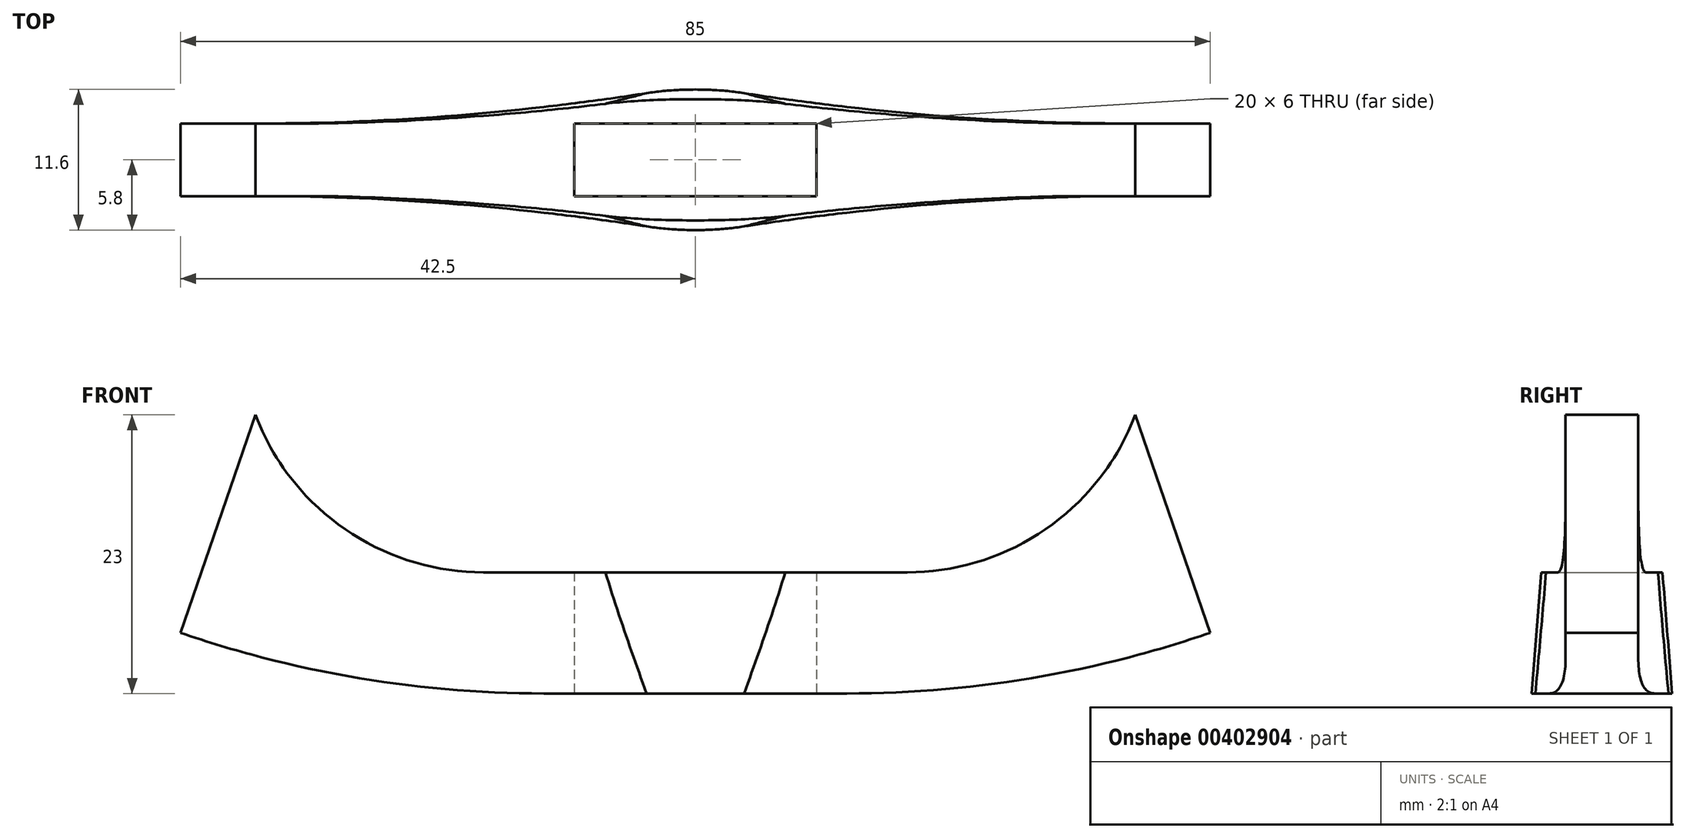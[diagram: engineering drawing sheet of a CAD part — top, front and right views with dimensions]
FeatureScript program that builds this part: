
annotation { "Feature Type Name" : "Feature", "Feature Type Description" : "" }
export const myFeature = defineFeature(function(context is Context, id is Id, definition is map)
    precondition{}
    {
        {
            var Q0;
            Q0=qCreatedBy(makeId("Front.planeOp"),FACE);
            var sketch = newSketch(context, id + "F0", { "sketchPlane" : qUnion([Q0])});
            skLineSegment(sketch, "E0", {"start": v(-15, 10) * mm, "end": v(-15, 0) * mm});
            skLineSegment(sketch, "E1", {"start": v(-15, 0) * mm, "end": v(-10, 0) * mm});
            skLineSegment(sketch, "E2", {"start": v(-10, 0) * mm, "end": v(-10, -10) * mm});
            skLineSegment(sketch, "E3", {"start": v(-10, -10) * mm, "end": v(-7.5, -10) * mm});
            skLineSegment(sketch, "E4", {"start": v(-7.5, -10) * mm, "end": v(-7.5, -30) * mm});
            skLineSegment(sketch, "E5", {"start": v(-7.5, -30) * mm, "end": v(0, -30) * mm});
            skLineSegment(sketch, "E6", {"start": v(0, -30) * mm, "end": v(7.5, -30) * mm});
            skLineSegment(sketch, "E7", {"start": v(7.5, -30) * mm, "end": v(7.5, -10) * mm});
            skLineSegment(sketch, "E8", {"start": v(7.5, -10) * mm, "end": v(10, -10) * mm});
            skLineSegment(sketch, "E9", {"start": v(10, -10) * mm, "end": v(10, 0) * mm});
            skLineSegment(sketch, "E10", {"start": v(10, 0) * mm, "end": v(15, 0) * mm});
            skLineSegment(sketch, "E11", {"start": v(15, 0) * mm, "end": v(15, 10) * mm});
            skLineSegment(sketch, "E12", {"start": v(15, 10) * mm, "end": v(-15, 10) * mm, "construction": true});
            skLineSegment(sketch, "E13", {"start": v(-15, 10) * mm, "end": v(0, 35.98) * mm});
            skLineSegment(sketch, "E14", {"start": v(0, 35.98) * mm, "end": v(15, 10) * mm});
            skSolve(sketch);
        }
        {
            var Q0;
            Q0=qCreatedBy(makeId("Front.planeOp"),FACE);
            var sketch = newSketch(context, id + "F1", { "sketchPlane" : qUnion([Q0])});
            skLineSegment(sketch, "E15", {"start": v(0, 0) * mm, "end": v(-17.5, 0) * mm});
            skLineSegment(sketch, "E16", {"start": v(-17.5, 0) * mm, "end": v(-12.5, -10) * mm, "construction": true});
            skLineSegment(sketch, "E17", {"start": v(-12.5, -10) * mm, "end": v(0, -10) * mm});
            skLineSegment(sketch, "E18", {"start": v(0, -10) * mm, "end": v(0, 0) * mm});
            skArc(sketch, "E19", {"start": v(-36.33, 13) * mm, "mid": v(-28.94, 3.57) * mm, "end": v(-17.5, 0) * mm});
            skArc(sketch, "E20", {"start": v(-42.5, -5) * mm, "mid": v(-27.7, -8.74) * mm, "end": v(-12.5, -10) * mm});
            skLineSegment(sketch, "E21", {"start": v(-42.5, -5) * mm, "end": v(-36.33, 13) * mm});
            skSolve(sketch);
        }
        {
            var Q0;
            Q0=qCreatedBy(makeId("Top.planeOp"),FACE);
            cPlane(context, id + "F2", {"entities" : qUnion([Q0]), "cplaneType" : CPlaneType.OFFSET, "offset" : 10 * mm, "oppositeDirection" : true, "width" : 150 * mm, "height" : 150 * mm});
        }
        {
            var Q0;
            Q0=qCreatedBy(id+"F2.planeOp",FACE);
            var sketch = newSketch(context, id + "F3", { "sketchPlane" : qUnion([Q0])});
            skLineSegment(sketch, "E22", {"start": v(0, 0) * mm, "end": v(-12.5, 0) * mm});
            skLineSegment(sketch, "E23", {"start": v(0, 0) * mm, "end": v(0, -5.8) * mm});
            skFitSpline(sketch, "E24", {"points": [v(-12.5, 0) * mm, v(-8.5, -4.3) * mm, v(0, -5.8) * mm], "startDerivative": vector(0, -14.6) * mm, "endDerivative": vector(16.42, 0) * mm});
            skSolve(sketch);
        }
        {
            var Q0;
            Q0=qCreatedBy(makeId("Top.planeOp"),FACE);
            var sketch = newSketch(context, id + "F4", { "sketchPlane" : qUnion([Q0])});
            skLineSegment(sketch, "E25", {"start": v(0, 0) * mm, "end": v(0, -5) * mm});
            skLineSegment(sketch, "E26", {"start": v(0, 0) * mm, "end": v(-17.5, 0) * mm});
            skFitSpline(sketch, "E27", {"points": [v(-17.5, 0) * mm, v(-14, -3) * mm, v(0, -5) * mm], "startDerivative": vector(0, -8.25) * mm, "endDerivative": vector(28.28, 0) * mm});
            skSolve(sketch);
        }
        {
            var Q0;
            Q0=makeQuery(id+"F4.imprint","IMPRINT",FACE,{"disambiguationData":[TD([[makeQuery(id+"F4.imprint","IMPRINT",EDGE,{"derivedFrom":sQuery(id+"F4.wireOp",EDGE,"E25")}),-1.0]])]});
            var Q1;
            Q1=makeQuery(id+"F3.imprint","IMPRINT",FACE,{"disambiguationData":[TD([[makeQuery(id+"F3.imprint","IMPRINT",EDGE,{"derivedFrom":sQuery(id+"F3.wireOp",EDGE,"E22")}),1.0]])]});
            loft(context, id + "F5", {"sheetProfilesArray" : [{ "sheetProfileEntities" : qUnion([Q0]) }, { "sheetProfileEntities" : qUnion([Q1]) }]});
        }
        {
            var Q0;
            Q0=makeQuery(id+"F1.imprint","IMPRINT",FACE,{"disambiguationData":[TD([[makeQuery(id+"F1.imprint","IMPRINT",EDGE,{"derivedFrom":sQuery(id+"F1.wireOp",EDGE,"E15")}),1.0]])]});
            extrude(context, id + "F6", {"entities" : qUnion([Q0]), "operationType" : NewBodyOperationType.ADD, "depth" : 3 * mm});
        }
        {
            var Q0;
            Q0=makeQuery(id+"F0.imprint","IMPRINT",FACE,{"disambiguationData":[TD([[makeQuery(id+"F0.imprint","IMPRINT",EDGE,{"derivedFrom":sQuery(id+"F0.wireOp",EDGE,"E0")}),1.0]])]});
            extrude(context, id + "F7", {"entities" : qUnion([Q0]), "operationType" : NewBodyOperationType.REMOVE, "depth" : 3 * mm});
        }
        {
            var Q0;
            {var subQ0=sQuery(id+"F4.wireOp",EDGE,"E27");var subQ1=sQuery(id+"F4.wireOp",EDGE,"E26");var subQ2=sQuery(id+"F4.wireOp",EDGE,"E25");var subQ3=sQuery(id+"F3.wireOp",EDGE,"E24");var subQ4=sQuery(id+"F3.wireOp",EDGE,"E23");var subQ5=sQuery(id+"F3.wireOp",EDGE,"E22");Q0=makeQuery(id+"F6.boolean.opBoolean","INTERSECT",EDGE,{"derivedFrom":[makeQuery(id+"F5.opLoft","SWEPT_FACE",FACE,{"disambiguationData":[OSD([subQ5,subQ4,subQ3,subQ2,subQ1,subQ0]),TDD([makeQuery(id+"F3.imprint","INTERSECT",VERTEX,{"derivedFrom":[subQ5,subQ3]}),makeQuery(id+"F3.imprint","INTERSECT",VERTEX,{"derivedFrom":[subQ4,subQ3]}),makeQuery(id+"F3.imprint","IMPRINT",EDGE,{"derivedFrom":subQ3}),makeQuery(id+"F4.imprint","INTERSECT",VERTEX,{"derivedFrom":[subQ2,subQ0]}),makeQuery(id+"F4.imprint","INTERSECT",VERTEX,{"derivedFrom":[subQ1,subQ0]}),makeQuery(id+"F4.imprint","IMPRINT",EDGE,{"derivedFrom":subQ0})])]}),makeQuery(id+"F6.opExtrude","CAP_FACE",FACE,{"disambiguationData":[OSD([sQuery(id+"F1.wireOp",EDGE,"E15"),sQuery(id+"F1.wireOp",EDGE,"E17"),sQuery(id+"F1.wireOp",EDGE,"E18"),sQuery(id+"F1.wireOp",EDGE,"E19"),sQuery(id+"F1.wireOp",EDGE,"E20"),sQuery(id+"F1.wireOp",EDGE,"E21")])],"isStart":false})]});}
            fillet(context, id + "F8", {"entities" : qUnion([Q0]), "radius" : 200 * mm, "tangentPropagation" : true, "allowEdgeOverflow" : false});
        }
        {
            var Q0;
            Q0=makeQuery(id+"F5.opLoft","SWEPT_BODY",BODY,{"disambiguationData":[OSD([makeQuery(id+"F3.imprint","IMPRINT",FACE,{"disambiguationData":[TD([[makeQuery(id+"F3.imprint","IMPRINT",EDGE,{"derivedFrom":sQuery(id+"F3.wireOp",EDGE,"E22")}),1.0]])]}),makeQuery(id+"F4.imprint","IMPRINT",FACE,{"disambiguationData":[TD([[makeQuery(id+"F4.imprint","IMPRINT",EDGE,{"derivedFrom":sQuery(id+"F4.wireOp",EDGE,"E25")}),-1.0]])]})])]});
            var Q1;
            {var subQ0=sQuery(id+"F4.wireOp",EDGE,"E26");var subQ1=sQuery(id+"F4.wireOp",EDGE,"E27");var subQ2=sQuery(id+"F4.wireOp",EDGE,"E25");var subQ3=sQuery(id+"F3.wireOp",EDGE,"E22");var subQ4=sQuery(id+"F3.wireOp",EDGE,"E24");var subQ5=sQuery(id+"F3.wireOp",EDGE,"E23");Q1=makeQuery(id+"F6.boolean.opBoolean","MERGE",FACE,{"derivedFrom":[makeQuery(id+"F5.opLoft","SWEPT_FACE",FACE,{"disambiguationData":[OSD([subQ3,subQ5,subQ4,subQ2,subQ0,subQ1]),TDD([makeQuery(id+"F3.imprint","INTERSECT",VERTEX,{"derivedFrom":[subQ3,subQ5]}),makeQuery(id+"F3.imprint","INTERSECT",VERTEX,{"derivedFrom":[subQ3,subQ4]}),makeQuery(id+"F3.imprint","IMPRINT",EDGE,{"derivedFrom":subQ3}),makeQuery(id+"F4.imprint","INTERSECT",VERTEX,{"derivedFrom":[subQ2,subQ0]}),makeQuery(id+"F4.imprint","INTERSECT",VERTEX,{"derivedFrom":[subQ0,subQ1]}),makeQuery(id+"F4.imprint","IMPRINT",EDGE,{"derivedFrom":subQ0})])]}),makeQuery(id+"F6.opExtrude","CAP_FACE",FACE,{"disambiguationData":[OSD([sQuery(id+"F1.wireOp",EDGE,"E15"),sQuery(id+"F1.wireOp",EDGE,"E17"),sQuery(id+"F1.wireOp",EDGE,"E18"),sQuery(id+"F1.wireOp",EDGE,"E19"),sQuery(id+"F1.wireOp",EDGE,"E20"),sQuery(id+"F1.wireOp",EDGE,"E21")])],"isStart":true})]});}
            mirror(context, id + "F9", {"operationType" : NewBodyOperationType.ADD, "entities" : qUnion([Q0]), "mirrorPlane" : qUnion([Q1])});
        }
        {
            var Q0;
            Q0=makeQuery(id+"F5.opLoft","SWEPT_BODY",BODY,{"disambiguationData":[OSD([makeQuery(id+"F3.imprint","IMPRINT",FACE,{"disambiguationData":[TD([[makeQuery(id+"F3.imprint","IMPRINT",EDGE,{"derivedFrom":sQuery(id+"F3.wireOp",EDGE,"E22")}),1.0]])]}),makeQuery(id+"F4.imprint","IMPRINT",FACE,{"disambiguationData":[TD([[makeQuery(id+"F4.imprint","IMPRINT",EDGE,{"derivedFrom":sQuery(id+"F4.wireOp",EDGE,"E25")}),-1.0]])]})])]});
            var Q1;
            {var subQ0=sQuery(id+"F4.wireOp",EDGE,"E25");var subQ1=sQuery(id+"F4.wireOp",EDGE,"E27");var subQ2=sQuery(id+"F4.wireOp",EDGE,"E26");var subQ3=sQuery(id+"F3.wireOp",EDGE,"E23");var subQ4=sQuery(id+"F3.wireOp",EDGE,"E24");var subQ5=sQuery(id+"F3.wireOp",EDGE,"E22");Q1=makeQuery(id+"F9.opPattern","COPY",FACE,{"derivedFrom":makeQuery(id+"F5.opLoft","SWEPT_FACE",FACE,{"disambiguationData":[OSD([subQ5,subQ3,subQ4,subQ0,subQ2,subQ1]),TDD([makeQuery(id+"F3.imprint","INTERSECT",VERTEX,{"derivedFrom":[subQ5,subQ3]}),makeQuery(id+"F3.imprint","INTERSECT",VERTEX,{"derivedFrom":[subQ3,subQ4]}),makeQuery(id+"F3.imprint","IMPRINT",EDGE,{"derivedFrom":subQ3}),makeQuery(id+"F4.imprint","INTERSECT",VERTEX,{"derivedFrom":[subQ0,subQ2]}),makeQuery(id+"F4.imprint","INTERSECT",VERTEX,{"derivedFrom":[subQ0,subQ1]}),makeQuery(id+"F4.imprint","IMPRINT",EDGE,{"derivedFrom":subQ0})])]}),"instanceName":"1"});}
            mirror(context, id + "F10", {"operationType" : NewBodyOperationType.ADD, "entities" : qUnion([Q0]), "mirrorPlane" : qUnion([Q1])});
        }
    });
